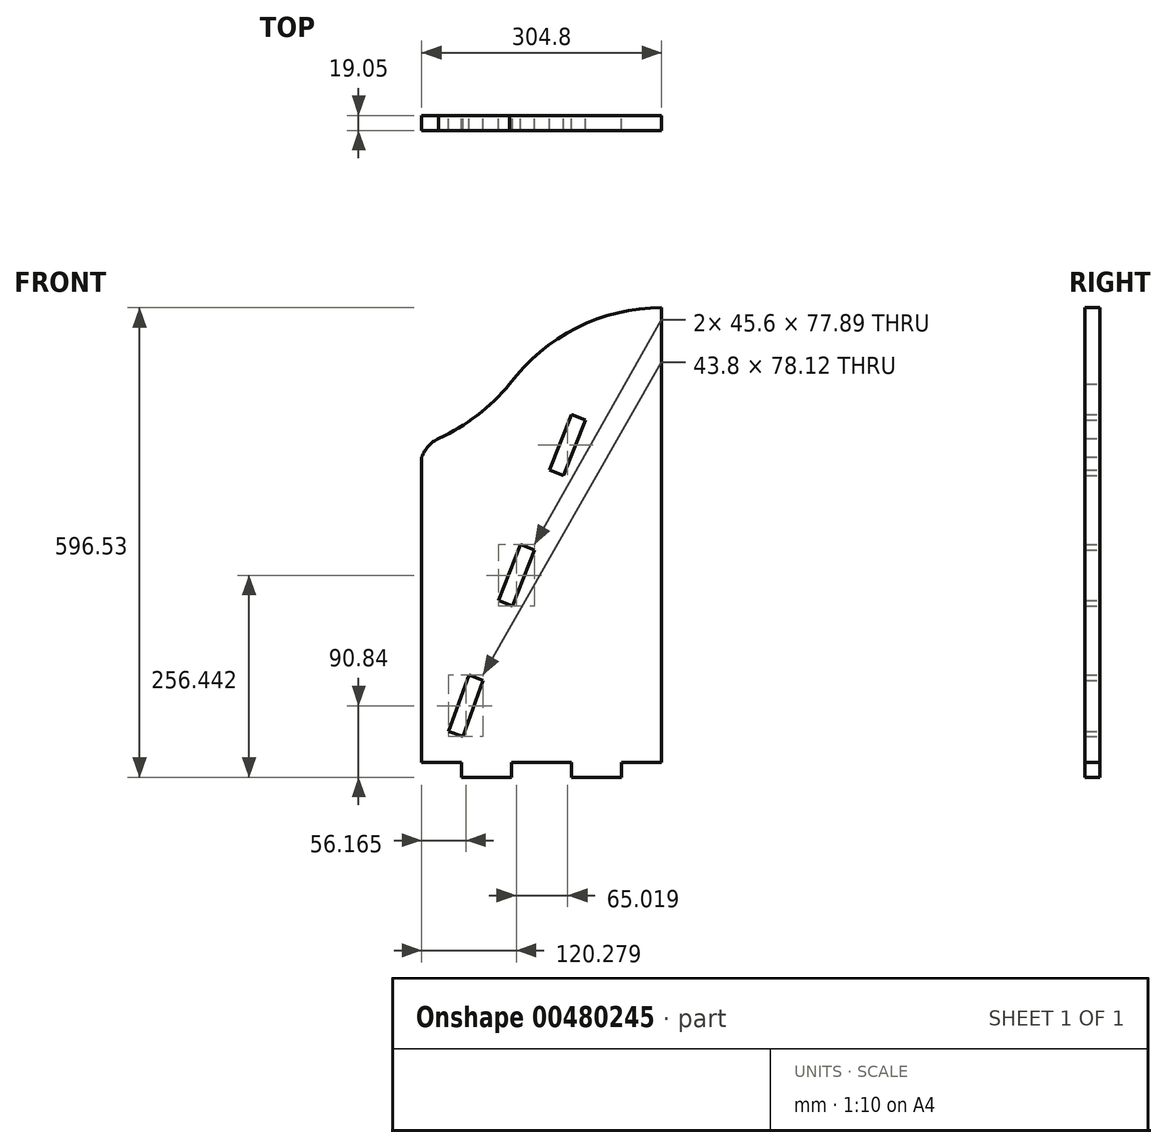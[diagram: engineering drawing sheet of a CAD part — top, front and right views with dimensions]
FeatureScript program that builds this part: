
annotation { "Feature Type Name" : "Feature", "Feature Type Description" : "" }
export const myFeature = defineFeature(function(context is Context, id is Id, definition is map)
    precondition{}
    {
        {
            var Q0;
            Q0=qCreatedBy(makeId("Front.planeOp"),FACE);
            var sketch = newSketch(context, id + "F0", { "sketchPlane" : qUnion([Q0])});
            skLineSegment(sketch, "E0.top", {"start": v(-137.72, -331.71) * mm, "end": v(-86.92, -331.71) * mm});
            skLineSegment(sketch, "E0.right", {"start": v(167.08, 262.22) * mm, "end": v(167.08, 261.08) * mm});
            skLineSegment(sketch, "E1.top", {"start": v(-86.92, -350.76) * mm, "end": v(-23.42, -350.76) * mm});
            skLineSegment(sketch, "E1.left", {"start": v(-86.92, -331.71) * mm, "end": v(-86.92, -350.76) * mm});
            skLineSegment(sketch, "E1.right", {"start": v(-23.42, -331.71) * mm, "end": v(-23.42, -350.76) * mm});
            skLineSegment(sketch, "E2.top", {"start": v(52.78, -350.76) * mm, "end": v(116.28, -350.76) * mm});
            skLineSegment(sketch, "E2.left", {"start": v(52.78, -331.71) * mm, "end": v(52.78, -350.76) * mm});
            skLineSegment(sketch, "E2.right", {"start": v(116.28, -331.71) * mm, "end": v(116.28, -350.76) * mm});
            skLineSegment(sketch, "E3.trimOffspring", {"start": v(-23.42, -331.71) * mm, "end": v(52.78, -331.71) * mm});
            skLineSegment(sketch, "E4.trimOffspring", {"start": v(116.28, -331.71) * mm, "end": v(167.08, -331.71) * mm});
            skLineSegment(sketch, "E5", {"start": v(-137.72, -331.71) * mm, "end": v(-137.72, -183.12) * mm});
            skArc(sketch, "E6", {"start": v(167.08, 261.08) * mm, "mid": v(167.1, 261.65) * mm, "end": v(167.08, 262.22) * mm});
            skLineSegment(sketch, "E7.trimOffspring", {"start": v(167.08, 245.77) * mm, "end": v(167.08, -331.71) * mm});
            skLineSegment(sketch, "E8", {"start": v(-137.72, 56.17) * mm, "end": v(-137.72, -183.12) * mm});
            skArc(sketch, "E9", {"start": v(167.08, 245.77) * mm, "mid": v(59.02, 220.06) * mm, "end": v(-25.9, 148.43) * mm});
            skArc(sketch, "E10", {"start": v(-116.1, 79.61) * mm, "mid": v(-67.16, 109) * mm, "end": v(-25.9, 148.43) * mm});
            skArc(sketch, "E11", {"start": v(-116.1, 79.61) * mm, "mid": v(-129.1, 69.92) * mm, "end": v(-137.72, 56.17) * mm});
            skLineSegment(sketch, "E12", {"start": v(-103.45, -292.46) * mm, "end": v(-77.4, -220.86) * mm});
            skLineSegment(sketch, "E13", {"start": v(-103.45, -292.46) * mm, "end": v(-85.55, -298.98) * mm});
            skLineSegment(sketch, "E14", {"start": v(-85.55, -298.98) * mm, "end": v(-59.66, -227.83) * mm});
            skLineSegment(sketch, "E15", {"start": v(-59.66, -227.83) * mm, "end": v(-77.4, -220.86) * mm});
            skLineSegment(sketch, "E16", {"start": v(-77.4, -220.86) * mm, "end": v(-40.24, -126.3) * mm, "construction": true});
            skLineSegment(sketch, "E17", {"start": v(-40.24, -126.3) * mm, "end": v(-12.37, -55.37) * mm});
            skLineSegment(sketch, "E18", {"start": v(-40.24, -126.3) * mm, "end": v(-22.5, -133.26) * mm});
            skLineSegment(sketch, "E19", {"start": v(-22.5, -133.26) * mm, "end": v(5.36, -62.34) * mm});
            skLineSegment(sketch, "E20", {"start": v(-12.37, -55.37) * mm, "end": v(5.36, -62.34) * mm});
            skLineSegment(sketch, "E21", {"start": v(-12.37, -55.37) * mm, "end": v(24.78, 39.19) * mm, "construction": true});
            skLineSegment(sketch, "E22", {"start": v(24.78, 39.19) * mm, "end": v(52.65, 110.11) * mm});
            skLineSegment(sketch, "E23", {"start": v(24.78, 39.19) * mm, "end": v(42.51, 32.22) * mm});
            skLineSegment(sketch, "E24", {"start": v(42.51, 32.22) * mm, "end": v(70.38, 103.15) * mm});
            skLineSegment(sketch, "E25", {"start": v(70.38, 103.15) * mm, "end": v(52.65, 110.11) * mm});
            skSolve(sketch);
        }
        {
            var Q0;
            Q0=makeQuery(id+"F0.imprint","IMPRINT",FACE,{"disambiguationData":[TD([[makeQuery(id+"F0.imprint","IMPRINT",EDGE,{"derivedFrom":sQuery(id+"F0.wireOp",EDGE,"E0.top")}),1.0]])]});
            extrude(context, id + "F1", {"entities" : qUnion([Q0]), "depth" : 19.05 * mm});
        }
    });
